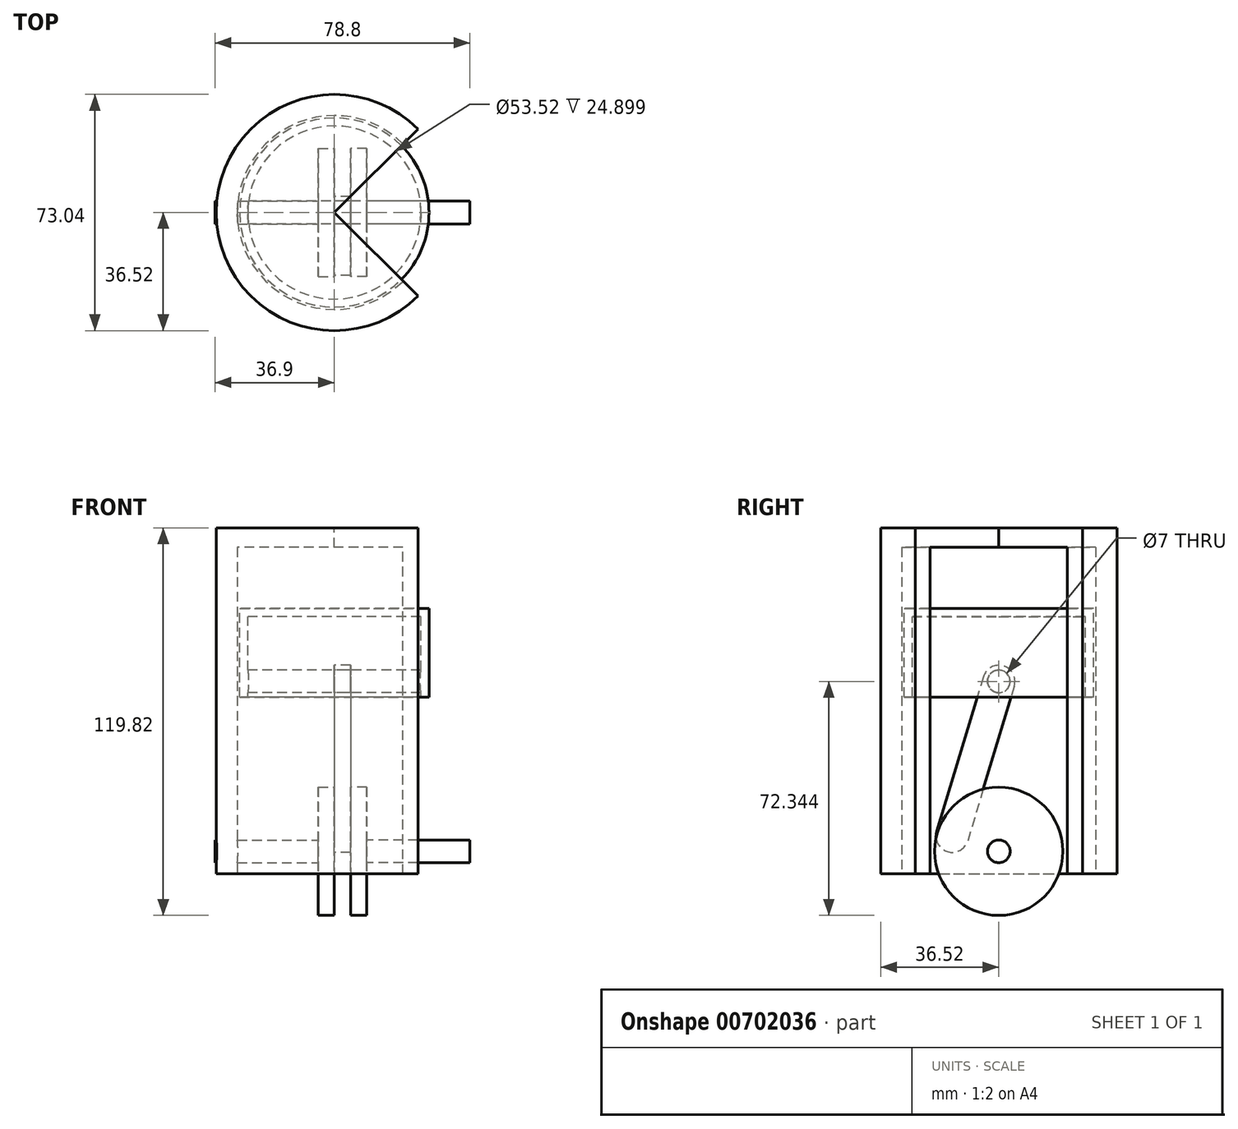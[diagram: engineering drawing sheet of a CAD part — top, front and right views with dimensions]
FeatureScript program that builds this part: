
annotation { "Feature Type Name" : "Feature", "Feature Type Description" : "" }
export const myFeature = defineFeature(function(context is Context, id is Id, definition is map)
    precondition{}
    {
        {
            var Q0;
            Q0=qCreatedBy(makeId("Front.planeOp"),FACE);
            var sketch = newSketch(context, id + "F0", { "sketchPlane" : qUnion([Q0])});
            skLineSegment(sketch, "E0", {"start": v(-30, -7) * mm, "end": v(-30, 94) * mm});
            skLineSegment(sketch, "E1", {"start": v(-30, 94) * mm, "end": v(0, 94) * mm});
            skLineSegment(sketch, "E2", {"start": v(0, 94) * mm, "end": v(0, 100) * mm});
            skLineSegment(sketch, "E3", {"start": v(0, 100) * mm, "end": v(-36.52, 100) * mm});
            skLineSegment(sketch, "E4", {"start": v(-36.52, 100) * mm, "end": v(-36.52, -7) * mm});
            skLineSegment(sketch, "E5", {"start": v(-36.52, -7) * mm, "end": v(-30, -7) * mm});
            skLineSegment(sketch, "E6", {"start": v(-57.06, 0) * mm, "end": v(24.04, 0) * mm, "construction": true});
            skSolve(sketch);
        }
        {
            var Q0;
            Q0=makeQuery(id+"F0.imprint","IMPRINT",FACE,{"disambiguationData":[TD([[makeQuery(id+"F0.imprint","IMPRINT",EDGE,{"derivedFrom":sQuery(id+"F0.wireOp",EDGE,"E0")}),1.0]])]});
            var Q1;
            Q1=sQuery(id+"F0.wireOp",EDGE,"E2");
            revolve(context, id + "F1", {"entities" : qUnion([Q0]), "axis" : qUnion([Q1]), "revolveType" : RevolveType.SYMMETRIC, "angle" : 270 * degree});
        }
        {
            var Q0;
            Q0=qCreatedBy(makeId("Right.planeOp"),FACE);
            var sketch = newSketch(context, id + "F2", { "sketchPlane" : qUnion([Q0])});
            skCircle(sketch, "E7", {"center": v(0, 0) * mm, "radius": 3.5 * mm});
            skSolve(sketch);
        }
        {
            var Q0;
            Q0 = qSketchRegion(id + "F2", true);
            extrude(context, id + "F3", {"entities" : qUnion([Q0]), "operationType" : NewBodyOperationType.REMOVE, "endBound" : BoundingType.THROUGH_ALL, "oppositeDirection" : true, "depth" : 25 * mm, "offsetDistance" : 25 * mm});
        }
        {
            var Q0;
            Q0=qCreatedBy(makeId("Right.planeOp"),FACE);
            var sketch = newSketch(context, id + "F4", { "sketchPlane" : qUnion([Q0])});
            skCircle(sketch, "E8", {"center": v(0, 0) * mm, "radius": 3.5 * mm});
            skSolve(sketch);
        }
        {
            var Q0;
            Q0 = qSketchRegion(id + "F4", true);
            extrude(context, id + "F5", {"entities" : qUnion([Q0]), "oppositeDirection" : true, "depth" : 36.9 * mm, "offsetDistance" : 25 * mm});
        }
        {
            var Q0;
            Q0=makeQuery(id+"F5.opExtrude","CAP_FACE",FACE,{"disambiguationData":[OSD([sQuery(id+"F4.wireOp",EDGE,"E8")])],"isStart":true});
            var sketch = newSketch(context, id + "F6", { "sketchPlane" : qUnion([Q0])});
            skCircle(sketch, "E9", {"center": v(0, 0) * mm, "radius": 19.82 * mm});
            skSolve(sketch);
        }
        {
            var Q0;
            Q0 = qSketchRegion(id + "F6", true);
            extrude(context, id + "F7", {"entities" : qUnion([Q0]), "operationType" : NewBodyOperationType.ADD, "oppositeDirection" : true, "depth" : 5 * mm, "offsetDistance" : 25 * mm});
        }
        {
            var Q0;
            Q0=makeQuery(id+"F7.boolean.opBoolean","MERGE",FACE,{"derivedFrom":[makeQuery(id+"F5.opExtrude","CAP_FACE",FACE,{"disambiguationData":[OSD([sQuery(id+"F4.wireOp",EDGE,"E8")])],"isStart":true}),makeQuery(id+"F7.opExtrude","CAP_FACE",FACE,{"disambiguationData":[OSD([sQuery(id+"F6.wireOp",EDGE,"E9")])],"isStart":true})]});
            var sketch = newSketch(context, id + "F8", { "sketchPlane" : qUnion([Q0])});
            skCircle(sketch, "E10", {"center": v(-14.4, 4.67) * mm, "radius": 3.5 * mm});
            skSolve(sketch);
        }
        {
            var Q0;
            Q0 = qSketchRegion(id + "F8", true);
            extrude(context, id + "F9", {"entities" : qUnion([Q0]), "operationType" : NewBodyOperationType.ADD, "depth" : 2.5 * mm, "offsetDistance" : 25 * mm});
        }
        {
            var Q0;
            Q0=qCreatedBy(makeId("Front.planeOp"),FACE);
            var sketch = newSketch(context, id + "F10", { "sketchPlane" : qUnion([Q0])});
            skLineSegment(sketch, "E11.bottom", {"start": v(0, 75.1) * mm, "end": v(-29.26, 75.1) * mm});
            skLineSegment(sketch, "E11.top", {"start": v(0, 47.7) * mm, "end": v(-29.26, 47.7) * mm});
            skLineSegment(sketch, "E11.left", {"start": v(0, 75.1) * mm, "end": v(0, 47.7) * mm});
            skLineSegment(sketch, "E11.right", {"start": v(-29.26, 75.1) * mm, "end": v(-29.26, 47.7) * mm});
            skSolve(sketch);
        }
        {
            var Q0;
            Q0=makeQuery(id+"F10.imprint","IMPRINT",FACE,{"disambiguationData":[TD([[makeQuery(id+"F10.imprint","IMPRINT",EDGE,{"derivedFrom":sQuery(id+"F10.wireOp",EDGE,"E11.bottom")}),1.0]])]});
            var Q1;
            Q1=sQuery(id+"F10.wireOp",EDGE,"E11.left");
            revolve(context, id + "F11", {"entities" : qUnion([Q0]), "axis" : qUnion([Q1]), "revolveType" : RevolveType.FULL});
        }
        {
            var Q0;
            Q0=makeQuery(id+"F11.opRevolve","SWEPT_FACE",FACE,{"disambiguationData":[OSD([sQuery(id+"F10.wireOp",EDGE,"E11.top")])]});
            shell(context, id + "F12", {"entities" : qUnion([Q0]), "thickness" : 2.5 * mm});
        }
        {
            var Q0;
            Q0=qCreatedBy(makeId("Right.planeOp"),FACE);
            var sketch = newSketch(context, id + "F13", { "sketchPlane" : qUnion([Q0])});
            skCircle(sketch, "E12", {"center": v(0, 52.52) * mm, "radius": 3.5 * mm});
            skSolve(sketch);
        }
        {
            var Q0;
            Q0 = qSketchRegion(id + "F13", true);
            extrude(context, id + "F14", {"entities" : qUnion([Q0]), "operationType" : NewBodyOperationType.ADD, "depth" : 57.6 * mm, "offsetDistance" : 25 * mm, "symmetric" : true});
        }
        {
            var Q0;
            Q0=qCreatedBy(makeId("Right.planeOp"),FACE);
            var sketch = newSketch(context, id + "F15", { "sketchPlane" : qUnion([Q0])});
            skCircle(sketch, "E13.0", {"center": v(-14.4, 4.67) * mm, "radius": 3.5 * mm});
            skCircle(sketch, "E14.0", {"center": v(0, 52.52) * mm, "radius": 3.5 * mm});
            skCircle(sketch, "E15", {"center": v(0, 52.52) * mm, "radius": 5 * mm});
            skCircle(sketch, "E16", {"center": v(-14.4, 4.67) * mm, "radius": 5 * mm});
            skLineSegment(sketch, "E17", {"start": v(-4.79, 53.96) * mm, "end": v(-19.18, 6.11) * mm});
            skLineSegment(sketch, "E18", {"start": v(4.79, 51.08) * mm, "end": v(-9.6, 3.23) * mm});
            skSolve(sketch);
        }
        {
            var Q0;
            Q0 = qSketchRegion(id + "F15", true);
            extrude(context, id + "F16", {"entities" : qUnion([Q0]), "depth" : 5 * mm, "offsetDistance" : 25 * mm});
        }
        {
            var Q0;
            Q0=makeQuery(id+"F5.opExtrude","SWEPT_BODY",BODY,{"disambiguationData":[OSD([sQuery(id+"F4.wireOp",EDGE,"E8")])]});
            var Q1;
            Q1=makeQuery(id+"F9.opExtrude","CAP_FACE",FACE,{"disambiguationData":[OSD([sQuery(id+"F8.wireOp",EDGE,"E10")])],"isStart":false});
            mirror(context, id + "F17", {"operationType" : NewBodyOperationType.ADD, "entities" : qUnion([Q0]), "mirrorPlane" : qUnion([Q1])});
        }
    });
